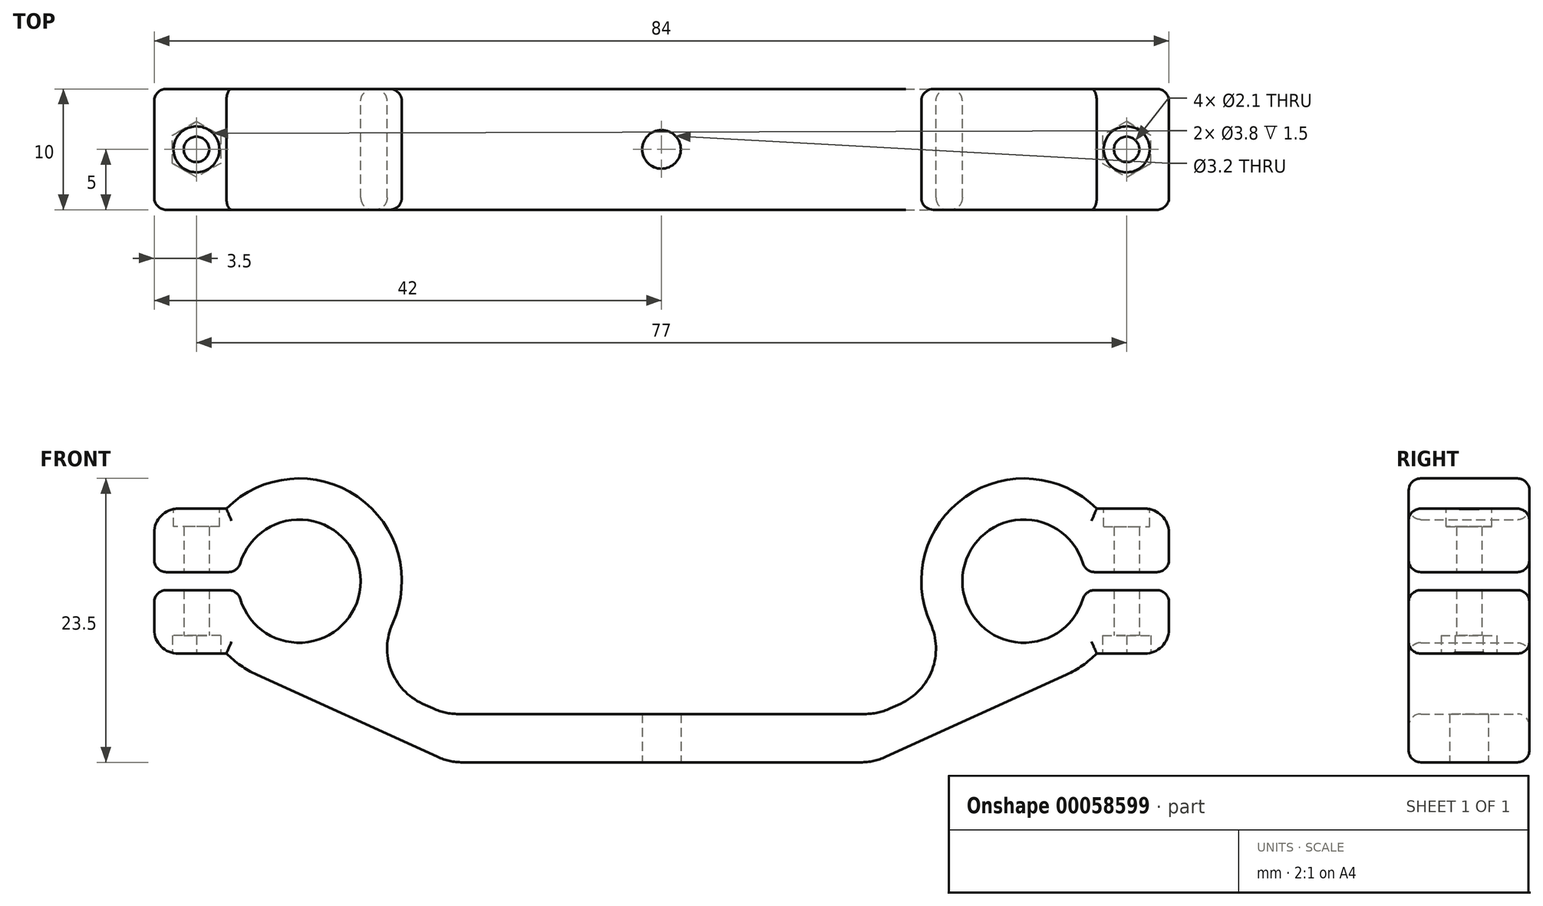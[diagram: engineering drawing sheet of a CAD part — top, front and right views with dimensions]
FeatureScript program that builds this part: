
annotation { "Feature Type Name" : "Feature", "Feature Type Description" : "" }
export const myFeature = defineFeature(function(context is Context, id is Id, definition is map)
    precondition{}
    {
        {
            var Q0;
            Q0=qCreatedBy(makeId("Front.planeOp"),FACE);
            var sketch = newSketch(context, id + "F0", { "sketchPlane" : qUnion([Q0])});
            skArc(sketch, "E0", {"start": v(-35.04, -0.75) * mm, "mid": v(-24.9, 0) * mm, "end": v(-35.04, 0.75) * mm});
            skArc(sketch, "E1", {"start": v(-36.02, -6) * mm, "mid": v(-34.85, -6.98) * mm, "end": v(-33.52, -7.74) * mm});
            skLineSegment(sketch, "E2", {"start": v(0, -15) * mm, "end": v(-17.57, -15) * mm});
            skLineSegment(sketch, "E3", {"start": v(-17.57, -15) * mm, "end": v(-33.52, -7.74) * mm});
            skLineSegment(sketch, "E4", {"start": v(0, -11) * mm, "end": v(-17.9, -11) * mm});
            skLineSegment(sketch, "E5", {"start": v(-17.9, -11) * mm, "end": v(-25.82, -7.4) * mm});
            skLineSegment(sketch, "E6.bottom", {"start": v(-42, 6) * mm, "end": v(-36.02, 6) * mm});
            skLineSegment(sketch, "E6.top", {"start": v(-42, -6) * mm, "end": v(-36.02, -6) * mm});
            skLineSegment(sketch, "E6.left", {"start": v(-42, 6) * mm, "end": v(-42, 0.75) * mm});
            skLineSegment(sketch, "E7.bottom", {"start": v(-42, 0.75) * mm, "end": v(-35.04, 0.75) * mm});
            skLineSegment(sketch, "E7.top", {"start": v(-42, -0.75) * mm, "end": v(-35.04, -0.75) * mm});
            skLineSegment(sketch, "E8.trimOffspring", {"start": v(-42, -0.75) * mm, "end": v(-42, -6) * mm});
            skArc(sketch, "E9.trimOffspring", {"start": v(-25.82, -7.4) * mm, "mid": v(-23.24, 5.15) * mm, "end": v(-36.02, 6) * mm});
            skLineSegment(sketch, "E10", {"start": v(0, -11) * mm, "end": v(0, -15) * mm});
            skSolve(sketch);
        }
        {
            var Q0;
            Q0=makeQuery(id+"F0.imprint","IMPRINT",FACE,{"disambiguationData":[TD([[makeQuery(id+"F0.imprint","IMPRINT",EDGE,{"derivedFrom":sQuery(id+"F0.wireOp",EDGE,"E0")}),-1.0]])]});
            extrude(context, id + "F1", {"entities" : qUnion([Q0]), "endBound" : BoundingType.SYMMETRIC, "depth" : 10 * mm});
        }
        {
            var Q0;
            Q0=makeQuery(id+"F1.opExtrude","SWEPT_EDGE",EDGE,{"disambiguationData":[OSD([sQuery(id+"F0.wireOp",EDGE,"E6.bottom"),sQuery(id+"F0.wireOp",EDGE,"E6.left")])]});
            var Q1;
            Q1=makeQuery(id+"F1.opExtrude","SWEPT_EDGE",EDGE,{"disambiguationData":[OSD([sQuery(id+"F0.wireOp",EDGE,"E6.top"),sQuery(id+"F0.wireOp",EDGE,"E8.trimOffspring")])]});
            var Q2;
            Q2=makeQuery(id+"F1.opExtrude","SWEPT_EDGE",EDGE,{"disambiguationData":[OSD([sQuery(id+"F0.wireOp",EDGE,"44421e0d-541d-4f5f-b472-7551b84f2a042.MirrorCS"),sQuery(id+"F0.wireOp",EDGE,"44421e0d-541d-4f5f-b472-7551b84f2a044.MirrorCS")])]});
            var Q3;
            Q3=makeQuery(id+"F1.opExtrude","SWEPT_EDGE",EDGE,{"disambiguationData":[OSD([sQuery(id+"F0.wireOp",EDGE,"44421e0d-541d-4f5f-b472-7551b84f2a043.MirrorCS"),sQuery(id+"F0.wireOp",EDGE,"44421e0d-541d-4f5f-b472-7551b84f2a047.MirrorCS")])]});
            fillet(context, id + "F2", {"entities" : qUnion([Q0, Q1, Q2, Q3]), "radius" : 2 * mm, "tangentPropagation" : true, "allowEdgeOverflow" : false});
        }
        {
            var Q0;
            Q0=makeQuery(id+"F1.opExtrude","SWEPT_EDGE",EDGE,{"disambiguationData":[OSD([sQuery(id+"F0.wireOp",EDGE,"E5"),sQuery(id+"F0.wireOp",EDGE,"E9.trimOffspring")])]});
            var Q1;
            Q1=makeQuery(id+"F1.opExtrude","SWEPT_EDGE",EDGE,{"disambiguationData":[OSD([sQuery(id+"F0.wireOp",EDGE,"E4"),sQuery(id+"F0.wireOp",EDGE,"E5")])]});
            var Q2;
            Q2=makeQuery(id+"F1.opExtrude","SWEPT_EDGE",EDGE,{"disambiguationData":[OSD([sQuery(id+"F0.wireOp",EDGE,"44421e0d-541d-4f5f-b472-7551b84f2a040.MirrorCS"),sQuery(id+"F0.wireOp",EDGE,"44421e0d-541d-4f5f-b472-7551b84f2a041.MirrorCS")])]});
            var Q3;
            Q3=makeQuery(id+"F1.opExtrude","SWEPT_EDGE",EDGE,{"disambiguationData":[OSD([sQuery(id+"F0.wireOp",EDGE,"44421e0d-541d-4f5f-b472-7551b84f2a041.MirrorCS"),sQuery(id+"F0.wireOp",EDGE,"44421e0d-541d-4f5f-b472-7551b84f2a048.MirrorCS")])]});
            var Q4;
            Q4=makeQuery(id+"F1.opExtrude","SWEPT_EDGE",EDGE,{"disambiguationData":[OSD([sQuery(id+"F0.wireOp",EDGE,"44421e0d-541d-4f5f-b472-7551b84f2a0410.MirrorCS"),sQuery(id+"F0.wireOp",EDGE,"44421e0d-541d-4f5f-b472-7551b84f2a0411.MirrorCS")])]});
            var Q5;
            Q5=makeQuery(id+"F1.opExtrude","SWEPT_EDGE",EDGE,{"disambiguationData":[OSD([sQuery(id+"F0.wireOp",EDGE,"E2"),sQuery(id+"F0.wireOp",EDGE,"E3")])]});
            fillet(context, id + "F3", {"entities" : qUnion([Q0, Q1, Q2, Q3, Q4, Q5]), "radius" : 5 * mm, "tangentPropagation" : true, "allowEdgeOverflow" : false});
        }
        {
            var Q0;
            Q0=makeQuery(id+"F1.opExtrude","SWEPT_FACE",FACE,{"disambiguationData":[OSD([sQuery(id+"F0.wireOp",EDGE,"E6.top")])]});
            var sketch = newSketch(context, id + "F4", { "sketchPlane" : qUnion([Q0])});
            skCircle(sketch, "E11.cCircle", {"center": v(-38.5, 0) * mm, "radius": 2 * mm, "construction": true});
            skLineSegment(sketch, "E11.0", {"start": v(-36.5, 1.15) * mm, "end": v(-36.5, -1.15) * mm});
            skLineSegment(sketch, "E11.1", {"start": v(-36.5, -1.15) * mm, "end": v(-38.5, -2.3) * mm});
            skLineSegment(sketch, "E11.2", {"start": v(-38.5, -2.3) * mm, "end": v(-40.5, -1.15) * mm});
            skLineSegment(sketch, "E11.3", {"start": v(-40.5, -1.15) * mm, "end": v(-40.5, 1.15) * mm});
            skLineSegment(sketch, "E11.4", {"start": v(-40.5, 1.15) * mm, "end": v(-38.5, 2.3) * mm});
            skLineSegment(sketch, "E11.5", {"start": v(-38.5, 2.3) * mm, "end": v(-36.5, 1.15) * mm});
            skPoint(sketch, "E11.0.midPoint", {"position": v(-36.5, 0) * mm});
            skCircle(sketch, "E12", {"center": v(-38.5, 0) * mm, "radius": 1.05 * mm});
            skSolve(sketch);
        }
        {
            var Q0;
            {var subQ1=sQuery(id+"F4.wireOp",EDGE,"E11.1");Q0=makeQuery(id+"F4.imprint","IMPRINT",FACE,{"disambiguationData":[TD([[makeQuery(id+"F4.imprint","IMPRINT",EDGE,{"derivedFrom":subQ1}),-1.0]])]});}
            var Q1;
            {var subQ0=sQuery(id+"F4.wireOp",EDGE,"E11.3");var subQ1=sQuery(id+"F4.wireOp",EDGE,"E11.2");var subQ2=makeQuery(id+"F4.imprint","INTERSECT",VERTEX,{"derivedFrom":[subQ1,subQ0]});Q1=makeQuery(id+"F4.imprint","IMPRINT",FACE,{"disambiguationData":[TD([[makeQuery(id+"F4.imprint","IMPRINT",EDGE,{"disambiguationData":[TD([[subQ2,1.0]])],"derivedFrom":subQ1}),-1.0]])]});}
            var Q2;
            {var subQ0=sQuery(id+"F4.wireOp",EDGE,"E11.5");var subQ1=sQuery(id+"F4.wireOp",EDGE,"E11.0");var subQ2=makeQuery(id+"F4.imprint","INTERSECT",VERTEX,{"derivedFrom":[subQ1,subQ0]});Q2=makeQuery(id+"F4.imprint","IMPRINT",FACE,{"disambiguationData":[TD([[makeQuery(id+"F4.imprint","IMPRINT",EDGE,{"disambiguationData":[TD([[subQ2,-1.0]])],"derivedFrom":subQ1}),-1.0]])]});}
            var Q3;
            Q3=makeQuery(id+"F4.imprint","IMPRINT",FACE,{"disambiguationData":[TD([[makeQuery(id+"F4.imprint","IMPRINT",EDGE,{"derivedFrom":sQuery(id+"F4.wireOp",EDGE,"E12")}),-1.0]])]});
            extrude(context, id + "F5", {"entities" : qUnion([Q0, Q1, Q2, Q3]), "operationType" : NewBodyOperationType.REMOVE, "endBound" : BoundingType.SYMMETRIC, "oppositeDirection" : true, "depth" : 3 * mm});
        }
        {
            var Q0;
            Q0=makeQuery(id+"F5.boolean.opBoolean","SPLIT",FACE,{"disambiguationData":[TD([makeQuery(id+"F5.opExtrude","SWEPT_FACE",FACE,{"disambiguationData":[OSD([sQuery(id+"F4.wireOp",EDGE,"E12")])]})])],"derivedFrom":makeQuery(id+"F1.opExtrude","SWEPT_FACE",FACE,{"disambiguationData":[OSD([sQuery(id+"F0.wireOp",EDGE,"E6.top")])]})});
            extrude(context, id + "F6", {"entities" : qUnion([Q0]), "operationType" : NewBodyOperationType.REMOVE, "endBound" : BoundingType.THROUGH_ALL, "oppositeDirection" : true, "depth" : 25 * mm});
        }
        {
            var Q0;
            Q0=makeQuery(id+"F1.opExtrude","SWEPT_FACE",FACE,{"disambiguationData":[OSD([sQuery(id+"F0.wireOp",EDGE,"E6.bottom")])]});
            var sketch = newSketch(context, id + "F7", { "sketchPlane" : qUnion([Q0])});
            skCircle(sketch, "E13.0", {"center": v(-38.5, 0) * mm, "radius": 1.05 * mm});
            skCircle(sketch, "E14", {"center": v(-38.5, 0) * mm, "radius": 1.9 * mm});
            skSolve(sketch);
        }
        {
            var Q0;
            Q0=makeQuery(id+"F7.imprint","IMPRINT",FACE,{"disambiguationData":[TD([[makeQuery(id+"F7.imprint","IMPRINT",EDGE,{"derivedFrom":sQuery(id+"F7.wireOp",EDGE,"E13.0")}),1.0]])]});
            var Q1;
            {var subQ0=sQuery(id+"F7.wireOp",EDGE,"E14");var subQ1=sQuery(id+"F0.wireOp",EDGE,"E6.bottom");var subQ2=makeQuery(id+"F2.opFillet","BLEND_EDGE",EDGE,{"blendedFrom":[makeQuery(id+"F1.opExtrude","SWEPT_EDGE",EDGE,{"disambiguationData":[OSD([subQ1,sQuery(id+"F0.wireOp",EDGE,"E6.left")])]}),makeQuery(id+"F1.opExtrude","SWEPT_FACE",FACE,{"disambiguationData":[OSD([subQ1])]})],"blendedInto":[makeQuery(id+"F1.opExtrude","SWEPT_FACE",FACE,{"disambiguationData":[OSD([subQ1])]})]});var subQ3=makeQuery(id+"F7.imprint","INTERSECT",VERTEX,{"disambiguationData":[OD(0.0)],"derivedFrom":[subQ2,subQ0]});Q1=makeQuery(id+"F7.imprint","IMPRINT",FACE,{"disambiguationData":[TD([[makeQuery(id+"F7.imprint","IMPRINT",EDGE,{"disambiguationData":[TD([[subQ3,-1.0]])],"derivedFrom":subQ0}),1.0]])]});}
            var Q2;
            {var subQ0=sQuery(id+"F7.wireOp",EDGE,"E14");var subQ1=makeQuery(id+"F1.opExtrude","SWEPT_EDGE",EDGE,{"disambiguationData":[OSD([sQuery(id+"F0.wireOp",EDGE,"E6.bottom"),sQuery(id+"F0.wireOp",EDGE,"E9.trimOffspring")])]});var subQ2=makeQuery(id+"F7.imprint","INTERSECT",VERTEX,{"disambiguationData":[OD(0.0)],"derivedFrom":[subQ1,subQ0]});Q2=makeQuery(id+"F7.imprint","IMPRINT",FACE,{"disambiguationData":[TD([[makeQuery(id+"F7.imprint","IMPRINT",EDGE,{"disambiguationData":[TD([[subQ2,1.0]])],"derivedFrom":subQ0}),1.0]])]});}
            extrude(context, id + "F8", {"entities" : qUnion([Q0, Q1, Q2]), "operationType" : NewBodyOperationType.REMOVE, "endBound" : BoundingType.SYMMETRIC, "oppositeDirection" : true, "depth" : 3 * mm});
        }
        {
            var Q0;
            Q0=makeQuery(id+"F1.opExtrude","SWEPT_EDGE",EDGE,{"disambiguationData":[OSD([sQuery(id+"F0.wireOp",EDGE,"E0"),sQuery(id+"F0.wireOp",EDGE,"E7.top")])]});
            var Q1;
            Q1=makeQuery(id+"F1.opExtrude","SWEPT_EDGE",EDGE,{"disambiguationData":[OSD([sQuery(id+"F0.wireOp",EDGE,"E0"),sQuery(id+"F0.wireOp",EDGE,"E7.bottom")])]});
            fillet(context, id + "F9", {"entities" : qUnion([Q0, Q1]), "radius" : 1 * mm, "tangentPropagation" : true, "allowEdgeOverflow" : false});
        }
        {
            var Q0;
            Q0=makeQuery(id+"F1.opExtrude","SWEPT_BODY",BODY,{"disambiguationData":[OSD([sQuery(id+"F0.wireOp",EDGE,"E0"),sQuery(id+"F0.wireOp",EDGE,"E1"),sQuery(id+"F0.wireOp",EDGE,"E2"),sQuery(id+"F0.wireOp",EDGE,"E3"),sQuery(id+"F0.wireOp",EDGE,"E4"),sQuery(id+"F0.wireOp",EDGE,"E5"),sQuery(id+"F0.wireOp",EDGE,"E6.bottom"),sQuery(id+"F0.wireOp",EDGE,"E6.top"),sQuery(id+"F0.wireOp",EDGE,"E6.left"),sQuery(id+"F0.wireOp",EDGE,"E7.bottom"),sQuery(id+"F0.wireOp",EDGE,"E7.top"),sQuery(id+"F0.wireOp",EDGE,"E8.trimOffspring"),sQuery(id+"F0.wireOp",EDGE,"E9.trimOffspring"),sQuery(id+"F0.wireOp",EDGE,"E10")])]});
            var Q1;
            Q1=qCreatedBy(makeId("Right.planeOp"),FACE);
            mirror(context, id + "F10", {"operationType" : NewBodyOperationType.ADD, "entities" : qUnion([Q0]), "mirrorPlane" : qUnion([Q1])});
        }
        {
            var Q0;
            {var subQ0=makeQuery(id+"F1.opExtrude","SWEPT_FACE",FACE,{"disambiguationData":[OSD([sQuery(id+"F0.wireOp",EDGE,"E2")])]});Q0=makeQuery(id+"F10.boolean.opBoolean","MERGE",FACE,{"derivedFrom":[subQ0,makeQuery(id+"F10.opPattern","COPY",FACE,{"derivedFrom":subQ0,"instanceName":"1"})]});}
            var sketch = newSketch(context, id + "F11", { "sketchPlane" : qUnion([Q0])});
            skCircle(sketch, "E15", {"center": v(0, 0) * mm, "radius": 1.6 * mm});
            skSolve(sketch);
        }
        {
            var Q0;
            Q0=makeQuery(id+"F11.imprint","IMPRINT",FACE,{"disambiguationData":[TD([[makeQuery(id+"F11.imprint","IMPRINT",EDGE,{"derivedFrom":sQuery(id+"F11.wireOp",EDGE,"E15")}),1.0]])]});
            extrude(context, id + "F12", {"entities" : qUnion([Q0]), "operationType" : NewBodyOperationType.REMOVE, "endBound" : BoundingType.THROUGH_ALL, "oppositeDirection" : true, "depth" : 25 * mm});
        }
        {
            var Q0;
            {var subQ0=makeQuery(id+"F1.opExtrude","CAP_EDGE",EDGE,{"disambiguationData":[OSD([sQuery(id+"F0.wireOp",EDGE,"E4")])],"isStart":false});Q0=makeQuery(id+"F10.boolean.opBoolean","MERGE",EDGE,{"derivedFrom":[subQ0,makeQuery(id+"F10.opPattern","COPY",EDGE,{"derivedFrom":subQ0,"instanceName":"1"})]});}
            var Q1;
            {var subQ0=makeQuery(id+"F1.opExtrude","CAP_EDGE",EDGE,{"disambiguationData":[OSD([sQuery(id+"F0.wireOp",EDGE,"E2")])],"isStart":false});Q1=makeQuery(id+"F10.boolean.opBoolean","MERGE",EDGE,{"derivedFrom":[subQ0,makeQuery(id+"F10.opPattern","COPY",EDGE,{"derivedFrom":subQ0,"instanceName":"1"})]});}
            var Q2;
            Q2=makeQuery(id+"F1.opExtrude","CAP_EDGE",EDGE,{"disambiguationData":[OSD([sQuery(id+"F0.wireOp",EDGE,"E0")])],"isStart":false});
            var Q3;
            Q3=makeQuery(id+"F10.opPattern","COPY",EDGE,{"derivedFrom":makeQuery(id+"F1.opExtrude","CAP_EDGE",EDGE,{"disambiguationData":[OSD([sQuery(id+"F0.wireOp",EDGE,"E0")])],"isStart":false}),"instanceName":"1"});
            var Q4;
            Q4=makeQuery(id+"F10.opPattern","COPY",EDGE,{"derivedFrom":makeQuery(id+"F1.opExtrude","CAP_EDGE",EDGE,{"disambiguationData":[OSD([sQuery(id+"F0.wireOp",EDGE,"E6.left")])],"isStart":false}),"instanceName":"1"});
            var Q5;
            Q5=makeQuery(id+"F10.opPattern","COPY",EDGE,{"derivedFrom":makeQuery(id+"F1.opExtrude","CAP_EDGE",EDGE,{"disambiguationData":[OSD([sQuery(id+"F0.wireOp",EDGE,"E8.trimOffspring")])],"isStart":false}),"instanceName":"1"});
            var Q6;
            Q6=makeQuery(id+"F1.opExtrude","CAP_EDGE",EDGE,{"disambiguationData":[OSD([sQuery(id+"F0.wireOp",EDGE,"E8.trimOffspring")])],"isStart":false});
            var Q7;
            Q7=makeQuery(id+"F1.opExtrude","CAP_EDGE",EDGE,{"disambiguationData":[OSD([sQuery(id+"F0.wireOp",EDGE,"E6.left")])],"isStart":false});
            var Q8;
            Q8=makeQuery(id+"F1.opExtrude","CAP_EDGE",EDGE,{"disambiguationData":[OSD([sQuery(id+"F0.wireOp",EDGE,"E6.left")])],"isStart":true});
            var Q9;
            Q9=makeQuery(id+"F1.opExtrude","CAP_EDGE",EDGE,{"disambiguationData":[OSD([sQuery(id+"F0.wireOp",EDGE,"E8.trimOffspring")])],"isStart":true});
            var Q10;
            Q10=makeQuery(id+"F1.opExtrude","CAP_EDGE",EDGE,{"disambiguationData":[OSD([sQuery(id+"F0.wireOp",EDGE,"E7.top")])],"isStart":true});
            var Q11;
            Q11=makeQuery(id+"F1.opExtrude","CAP_EDGE",EDGE,{"disambiguationData":[OSD([sQuery(id+"F0.wireOp",EDGE,"E3")])],"isStart":true});
            var Q12;
            {var subQ0=sQuery(id+"F0.wireOp",EDGE,"E9.trimOffspring");var subQ1=sQuery(id+"F0.wireOp",EDGE,"E5");Q12=makeQuery(id+"F3.opFillet","BLEND_EDGE",EDGE,{"blendedFrom":[makeQuery(id+"F1.opExtrude","SWEPT_EDGE",EDGE,{"disambiguationData":[OSD([subQ1,subQ0])]}),makeQuery(id+"F1.opExtrude","CAP_FACE",FACE,{"disambiguationData":[OSD([sQuery(id+"F0.wireOp",EDGE,"E0"),sQuery(id+"F0.wireOp",EDGE,"E1"),sQuery(id+"F0.wireOp",EDGE,"E2"),sQuery(id+"F0.wireOp",EDGE,"E3"),sQuery(id+"F0.wireOp",EDGE,"E4"),subQ1,sQuery(id+"F0.wireOp",EDGE,"E6.bottom"),sQuery(id+"F0.wireOp",EDGE,"E6.top"),sQuery(id+"F0.wireOp",EDGE,"E6.left"),sQuery(id+"F0.wireOp",EDGE,"E7.bottom"),sQuery(id+"F0.wireOp",EDGE,"E7.top"),sQuery(id+"F0.wireOp",EDGE,"E8.trimOffspring"),subQ0,sQuery(id+"F0.wireOp",EDGE,"E10")])],"isStart":true})],"blendedInto":[makeQuery(id+"F1.opExtrude","CAP_FACE",FACE,{"disambiguationData":[OSD([sQuery(id+"F0.wireOp",EDGE,"E0"),sQuery(id+"F0.wireOp",EDGE,"E1"),sQuery(id+"F0.wireOp",EDGE,"E2"),sQuery(id+"F0.wireOp",EDGE,"E3"),sQuery(id+"F0.wireOp",EDGE,"E4"),subQ1,sQuery(id+"F0.wireOp",EDGE,"E6.bottom"),sQuery(id+"F0.wireOp",EDGE,"E6.top"),sQuery(id+"F0.wireOp",EDGE,"E6.left"),sQuery(id+"F0.wireOp",EDGE,"E7.bottom"),sQuery(id+"F0.wireOp",EDGE,"E7.top"),sQuery(id+"F0.wireOp",EDGE,"E8.trimOffspring"),subQ0,sQuery(id+"F0.wireOp",EDGE,"E10")])],"isStart":true})]});}
            var Q13;
            Q13=makeQuery(id+"F10.opPattern","COPY",EDGE,{"derivedFrom":makeQuery(id+"F1.opExtrude","CAP_EDGE",EDGE,{"disambiguationData":[OSD([sQuery(id+"F0.wireOp",EDGE,"E6.left")])],"isStart":true}),"instanceName":"1"});
            var Q14;
            Q14=makeQuery(id+"F10.opPattern","COPY",EDGE,{"derivedFrom":makeQuery(id+"F1.opExtrude","CAP_EDGE",EDGE,{"disambiguationData":[OSD([sQuery(id+"F0.wireOp",EDGE,"E7.bottom")])],"isStart":true}),"instanceName":"1"});
            var Q15;
            Q15=makeQuery(id+"F10.opPattern","COPY",EDGE,{"derivedFrom":makeQuery(id+"F1.opExtrude","CAP_EDGE",EDGE,{"disambiguationData":[OSD([sQuery(id+"F0.wireOp",EDGE,"E8.trimOffspring")])],"isStart":true}),"instanceName":"1"});
            var Q16;
            Q16=makeQuery(id+"F10.opPattern","COPY",EDGE,{"derivedFrom":makeQuery(id+"F1.opExtrude","SWEPT_EDGE",EDGE,{"disambiguationData":[OSD([sQuery(id+"F0.wireOp",EDGE,"E7.top"),sQuery(id+"F0.wireOp",EDGE,"E8.trimOffspring")])]}),"instanceName":"1"});
            var Q17;
            Q17=makeQuery(id+"F10.opPattern","COPY",EDGE,{"derivedFrom":makeQuery(id+"F1.opExtrude","SWEPT_EDGE",EDGE,{"disambiguationData":[OSD([sQuery(id+"F0.wireOp",EDGE,"E6.left"),sQuery(id+"F0.wireOp",EDGE,"E7.bottom")])]}),"instanceName":"1"});
            var Q18;
            Q18=makeQuery(id+"F1.opExtrude","SWEPT_EDGE",EDGE,{"disambiguationData":[OSD([sQuery(id+"F0.wireOp",EDGE,"E6.left"),sQuery(id+"F0.wireOp",EDGE,"E7.bottom")])]});
            var Q19;
            Q19=makeQuery(id+"F1.opExtrude","SWEPT_EDGE",EDGE,{"disambiguationData":[OSD([sQuery(id+"F0.wireOp",EDGE,"E7.top"),sQuery(id+"F0.wireOp",EDGE,"E8.trimOffspring")])]});
            fillet(context, id + "F13", {"entities" : qUnion([Q0, Q1, Q2, Q3, Q4, Q5, Q6, Q7, Q8, Q9, Q10, Q11, Q12, Q13, Q14, Q15, Q16, Q17, Q18, Q19]), "radius" : 1 * mm, "tangentPropagation" : true, "allowEdgeOverflow" : false});
        }
    });
